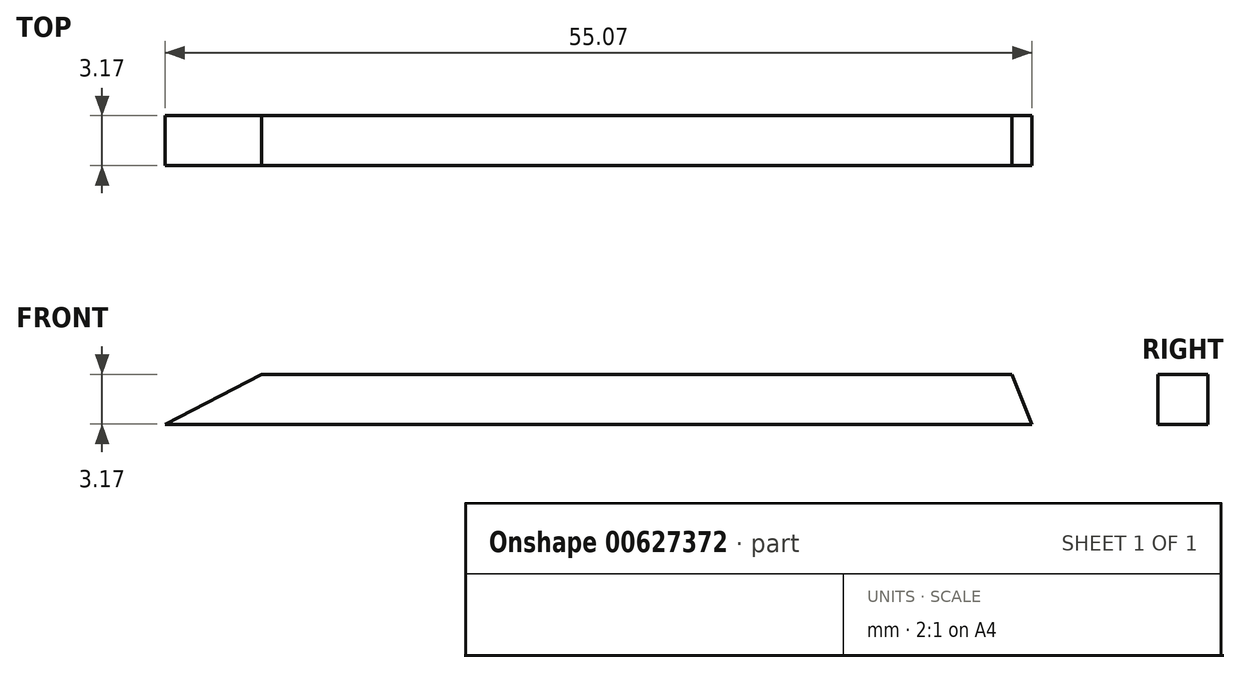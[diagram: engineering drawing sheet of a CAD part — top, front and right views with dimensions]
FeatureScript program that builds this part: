
annotation { "Feature Type Name" : "Feature", "Feature Type Description" : "" }
export const myFeature = defineFeature(function(context is Context, id is Id, definition is map)
    precondition{}
    {
        {
            var Q0;
            Q0=qCreatedBy(makeId("Front.planeOp"),FACE);
            var sketch = newSketch(context, id + "F0", { "sketchPlane" : qUnion([Q0])});
            skLineSegment(sketch, "E0", {"start": v(-108.78, -17.08) * mm, "end": v(-61.12, -17.08) * mm});
            skLineSegment(sketch, "E1", {"start": v(-61.12, -17.08) * mm, "end": v(-61.12, -20.25) * mm});
            skLineSegment(sketch, "E2", {"start": v(-61.12, -20.25) * mm, "end": v(-114.9, -20.25) * mm});
            skLineSegment(sketch, "E3", {"start": v(-114.9, -20.25) * mm, "end": v(-108.78, -17.08) * mm});
            skLineSegment(sketch, "E4", {"start": v(-61.12, -20.25) * mm, "end": v(-59.84, -20.25) * mm});
            skLineSegment(sketch, "E5", {"start": v(-59.84, -20.25) * mm, "end": v(-61.12, -17.08) * mm});
            skSolve(sketch);
        }
        {
            var Q0;
            Q0 = qSketchRegion(id + "F0", true);
            extrude(context, id + "F1", {"entities" : qUnion([Q0]), "depth" : 3.17 * mm, "offsetDistance" : 25.4 * mm});
        }
    });
